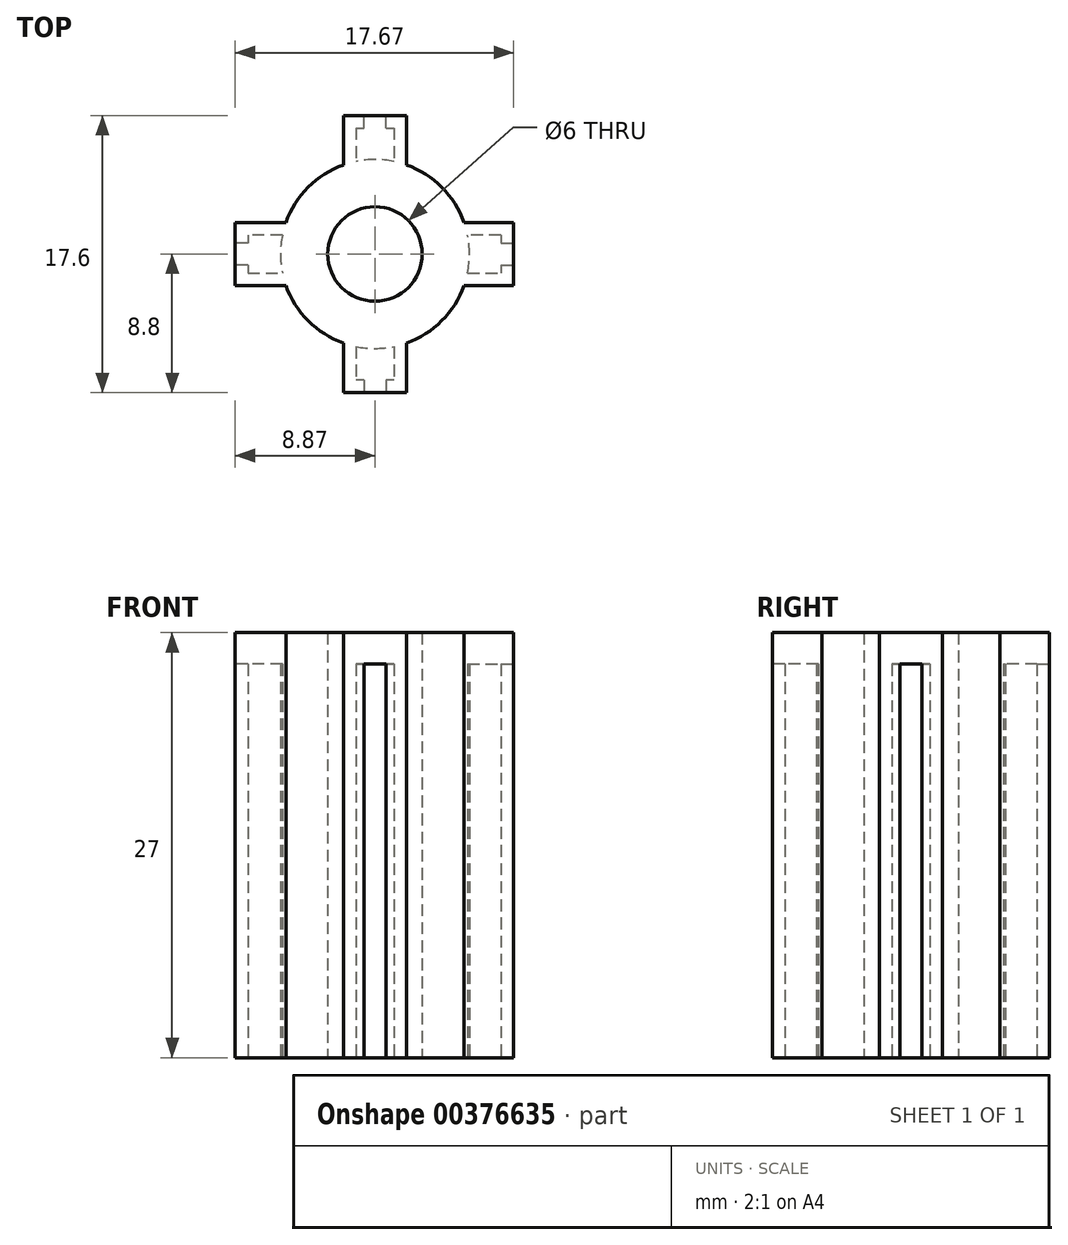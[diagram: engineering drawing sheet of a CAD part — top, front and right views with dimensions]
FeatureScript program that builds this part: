
annotation { "Feature Type Name" : "Feature", "Feature Type Description" : "" }
export const myFeature = defineFeature(function(context is Context, id is Id, definition is map)
    precondition{}
    {
        {
            var Q0;
            Q0=qCreatedBy(makeId("Top.planeOp"),FACE);
            var sketch = newSketch(context, id + "F0", { "sketchPlane" : qUnion([Q0])});
            skCircle(sketch, "E0", {"center": v(0, 0) * mm, "radius": 3 * mm});
            skArc(sketch, "E1", {"start": v(-5.88, 1.2) * mm, "mid": v(-6, 0) * mm, "end": v(-5.88, -1.2) * mm});
            skLineSegment(sketch, "E2.bottom", {"start": v(-8, -1.2) * mm, "end": v(-5.88, -1.2) * mm});
            skLineSegment(sketch, "E2.top", {"start": v(-8, -2) * mm, "end": v(-5.66, -2) * mm});
            skLineSegment(sketch, "E3.bottom", {"start": v(8, 1.2) * mm, "end": v(5.88, 1.2) * mm});
            skLineSegment(sketch, "E3.top", {"start": v(8, 2) * mm, "end": v(5.66, 2) * mm});
            skLineSegment(sketch, "E4.trimOffspring", {"start": v(-5.66, 2) * mm, "end": v(-8.07, 2) * mm});
            skLineSegment(sketch, "E5.trimOffspring", {"start": v(-5.88, 1.2) * mm, "end": v(-8.07, 1.2) * mm});
            skLineSegment(sketch, "E6.trimOffspring", {"start": v(5.88, -1.2) * mm, "end": v(8, -1.2) * mm});
            skLineSegment(sketch, "E7.trimOffspring", {"start": v(5.66, -2) * mm, "end": v(8, -2) * mm});
            skArc(sketch, "E8.trimOffspring", {"start": v(-5.66, -2) * mm, "mid": v(-4.24, -4.24) * mm, "end": v(-2, -5.66) * mm});
            skArc(sketch, "E9.trimOffspring", {"start": v(5.88, -1.2) * mm, "mid": v(6, 0) * mm, "end": v(5.88, 1.2) * mm});
            skArc(sketch, "E10.trimOffspring", {"start": v(5.66, 2) * mm, "mid": v(4.24, 4.24) * mm, "end": v(2, 5.66) * mm});
            skLineSegment(sketch, "E11.left", {"start": v(-1.2, 8) * mm, "end": v(-1.2, 5.88) * mm});
            skLineSegment(sketch, "E11.right", {"start": v(-2, 8) * mm, "end": v(-2, 5.66) * mm});
            skLineSegment(sketch, "E12.left", {"start": v(1.2, 8) * mm, "end": v(1.2, 5.88) * mm});
            skLineSegment(sketch, "E12.right", {"start": v(2, 8) * mm, "end": v(2, 5.66) * mm});
            skLineSegment(sketch, "E13.trimOffspring", {"start": v(-1.2, -5.88) * mm, "end": v(-1.2, -8) * mm});
            skLineSegment(sketch, "E14.trimOffspring", {"start": v(-2, -5.66) * mm, "end": v(-2, -8) * mm});
            skLineSegment(sketch, "E15.trimOffspring", {"start": v(1.2, -5.88) * mm, "end": v(1.2, -8) * mm});
            skLineSegment(sketch, "E16.trimOffspring", {"start": v(2, -5.66) * mm, "end": v(2, -8) * mm});
            skArc(sketch, "E17.trimOffspring", {"start": v(1.2, 5.88) * mm, "mid": v(0, 6) * mm, "end": v(-1.2, 5.88) * mm});
            skArc(sketch, "E18.trimOffspring", {"start": v(-2, 5.66) * mm, "mid": v(-4.24, 4.24) * mm, "end": v(-5.66, 2) * mm});
            skArc(sketch, "E19.trimOffspring", {"start": v(-1.2, -5.88) * mm, "mid": v(0, -6) * mm, "end": v(1.2, -5.88) * mm});
            skArc(sketch, "E20.trimOffspring", {"start": v(2, -5.66) * mm, "mid": v(4.24, -4.24) * mm, "end": v(5.66, -2) * mm});
            skLineSegment(sketch, "E21.bottom", {"start": v(8, 2) * mm, "end": v(8.8, 2) * mm});
            skLineSegment(sketch, "E21.top", {"start": v(8, -2) * mm, "end": v(8.8, -2) * mm});
            skLineSegment(sketch, "E21.left", {"start": v(8, 1.2) * mm, "end": v(8, 0.7) * mm});
            skLineSegment(sketch, "E21.right", {"start": v(8.8, 2) * mm, "end": v(8.8, 0.7) * mm});
            skLineSegment(sketch, "E22.bottom", {"start": v(-1.2, 8) * mm, "end": v(-0.7, 8) * mm});
            skLineSegment(sketch, "E22.top", {"start": v(-2, 8.8) * mm, "end": v(-0.7, 8.8) * mm});
            skLineSegment(sketch, "E22.left", {"start": v(-2, 8) * mm, "end": v(-2, 8.8) * mm});
            skLineSegment(sketch, "E22.right", {"start": v(2, 8) * mm, "end": v(2, 8.8) * mm});
            skLineSegment(sketch, "E23.bottom", {"start": v(-8.07, 2) * mm, "end": v(-8.87, 2) * mm});
            skLineSegment(sketch, "E23.top", {"start": v(-8.07, -2) * mm, "end": v(-8.87, -2) * mm});
            skLineSegment(sketch, "E23.left", {"start": v(-8.07, 1.2) * mm, "end": v(-8.07, 0.7) * mm});
            skLineSegment(sketch, "E23.right", {"start": v(-8.87, 2) * mm, "end": v(-8.87, 0.7) * mm});
            skLineSegment(sketch, "E24.bottom", {"start": v(1.2, -8) * mm, "end": v(0.7, -8) * mm});
            skLineSegment(sketch, "E24.top", {"start": v(2, -8.8) * mm, "end": v(0.7, -8.8) * mm});
            skLineSegment(sketch, "E24.left", {"start": v(2, -8) * mm, "end": v(2, -8.8) * mm});
            skLineSegment(sketch, "E24.right", {"start": v(-2, -8) * mm, "end": v(-2, -8.8) * mm});
            skLineSegment(sketch, "E25", {"start": v(0.7, -8) * mm, "end": v(0.7, -8.8) * mm});
            skLineSegment(sketch, "E26", {"start": v(-0.7, -8) * mm, "end": v(-0.7, -8.8) * mm});
            skLineSegment(sketch, "E27.trimOffspring", {"start": v(-0.7, -8) * mm, "end": v(-1.2, -8) * mm});
            skLineSegment(sketch, "E28.trimOffspring", {"start": v(-0.7, -8.8) * mm, "end": v(-2, -8.8) * mm});
            skLineSegment(sketch, "E29", {"start": v(8, 0.7) * mm, "end": v(8.8, 0.7) * mm});
            skLineSegment(sketch, "E30", {"start": v(8, -0.7) * mm, "end": v(8.8, -0.7) * mm});
            skLineSegment(sketch, "E31", {"start": v(-0.7, 8) * mm, "end": v(-0.7, 8.8) * mm});
            skLineSegment(sketch, "E32", {"start": v(0.7, 8) * mm, "end": v(0.7, 8.8) * mm});
            skLineSegment(sketch, "E33.trimOffspring", {"start": v(0.7, 8) * mm, "end": v(1.2, 8) * mm});
            skLineSegment(sketch, "E34.trimOffspring", {"start": v(0.7, 8.8) * mm, "end": v(2, 8.8) * mm});
            skLineSegment(sketch, "E35", {"start": v(-8.07, 0.7) * mm, "end": v(-8.87, 0.7) * mm});
            skLineSegment(sketch, "E36", {"start": v(-8.07, -0.7) * mm, "end": v(-8.87, -0.7) * mm});
            skLineSegment(sketch, "E37", {"start": v(-8, -1.2) * mm, "end": v(-8.07, -1.2) * mm});
            skLineSegment(sketch, "E38", {"start": v(-8, -2) * mm, "end": v(-8.07, -2) * mm});
            skLineSegment(sketch, "E39.trimOffspring", {"start": v(-8.07, -0.7) * mm, "end": v(-8.07, -1.2) * mm});
            skLineSegment(sketch, "E40.trimOffspring", {"start": v(-8.87, -0.7) * mm, "end": v(-8.87, -2) * mm});
            skLineSegment(sketch, "E41.trimOffspring", {"start": v(8.8, -0.7) * mm, "end": v(8.8, -2) * mm});
            skLineSegment(sketch, "E42.trimOffspring", {"start": v(8, -0.7) * mm, "end": v(8, -1.2) * mm});
            skSolve(sketch);
        }
        {
            var Q0;
            Q0=makeQuery(id+"F0.imprint","IMPRINT",FACE,{"disambiguationData":[TD([[makeQuery(id+"F0.imprint","IMPRINT",EDGE,{"derivedFrom":sQuery(id+"F0.wireOp",EDGE,"E0")}),-1.0]])]});
            extrude(context, id + "F1", {"entities" : qUnion([Q0]), "depth" : 25 * mm});
        }
        {
            var Q0;
            Q0=makeQuery(id+"F1.opExtrude","CAP_FACE",FACE,{"disambiguationData":[OSD([sQuery(id+"F0.wireOp",EDGE,"E0"),sQuery(id+"F0.wireOp",EDGE,"E1"),sQuery(id+"F0.wireOp",EDGE,"E2.bottom"),sQuery(id+"F0.wireOp",EDGE,"E2.top"),sQuery(id+"F0.wireOp",EDGE,"E3.bottom"),sQuery(id+"F0.wireOp",EDGE,"E3.top"),sQuery(id+"F0.wireOp",EDGE,"E4.trimOffspring"),sQuery(id+"F0.wireOp",EDGE,"E5.trimOffspring"),sQuery(id+"F0.wireOp",EDGE,"E6.trimOffspring"),sQuery(id+"F0.wireOp",EDGE,"E7.trimOffspring"),sQuery(id+"F0.wireOp",EDGE,"E8.trimOffspring"),sQuery(id+"F0.wireOp",EDGE,"E9.trimOffspring"),sQuery(id+"F0.wireOp",EDGE,"E10.trimOffspring"),sQuery(id+"F0.wireOp",EDGE,"E11.left"),sQuery(id+"F0.wireOp",EDGE,"E11.right"),sQuery(id+"F0.wireOp",EDGE,"E12.left"),sQuery(id+"F0.wireOp",EDGE,"E12.right"),sQuery(id+"F0.wireOp",EDGE,"E13.trimOffspring"),sQuery(id+"F0.wireOp",EDGE,"E14.trimOffspring"),sQuery(id+"F0.wireOp",EDGE,"E15.trimOffspring"),sQuery(id+"F0.wireOp",EDGE,"E16.trimOffspring"),sQuery(id+"F0.wireOp",EDGE,"E17.trimOffspring"),sQuery(id+"F0.wireOp",EDGE,"E18.trimOffspring"),sQuery(id+"F0.wireOp",EDGE,"E19.trimOffspring"),sQuery(id+"F0.wireOp",EDGE,"E20.trimOffspring"),sQuery(id+"F0.wireOp",EDGE,"E21.bottom"),sQuery(id+"F0.wireOp",EDGE,"E21.top"),sQuery(id+"F0.wireOp",EDGE,"E21.left"),sQuery(id+"F0.wireOp",EDGE,"E21.right"),sQuery(id+"F0.wireOp",EDGE,"E22.bottom"),sQuery(id+"F0.wireOp",EDGE,"E22.top"),sQuery(id+"F0.wireOp",EDGE,"E22.left"),sQuery(id+"F0.wireOp",EDGE,"E22.right"),sQuery(id+"F0.wireOp",EDGE,"E23.bottom"),sQuery(id+"F0.wireOp",EDGE,"E23.top"),sQuery(id+"F0.wireOp",EDGE,"E23.left"),sQuery(id+"F0.wireOp",EDGE,"E23.right"),sQuery(id+"F0.wireOp",EDGE,"E24.bottom"),sQuery(id+"F0.wireOp",EDGE,"E24.top"),sQuery(id+"F0.wireOp",EDGE,"E24.left"),sQuery(id+"F0.wireOp",EDGE,"E24.right"),sQuery(id+"F0.wireOp",EDGE,"E25"),sQuery(id+"F0.wireOp",EDGE,"E26"),sQuery(id+"F0.wireOp",EDGE,"E27.trimOffspring"),sQuery(id+"F0.wireOp",EDGE,"E28.trimOffspring"),sQuery(id+"F0.wireOp",EDGE,"E29"),sQuery(id+"F0.wireOp",EDGE,"E30"),sQuery(id+"F0.wireOp",EDGE,"E31"),sQuery(id+"F0.wireOp",EDGE,"E32"),sQuery(id+"F0.wireOp",EDGE,"E33.trimOffspring"),sQuery(id+"F0.wireOp",EDGE,"E34.trimOffspring"),sQuery(id+"F0.wireOp",EDGE,"E35"),sQuery(id+"F0.wireOp",EDGE,"E36"),sQuery(id+"F0.wireOp",EDGE,"E37"),sQuery(id+"F0.wireOp",EDGE,"E38"),sQuery(id+"F0.wireOp",EDGE,"E39.trimOffspring"),sQuery(id+"F0.wireOp",EDGE,"E40.trimOffspring"),sQuery(id+"F0.wireOp",EDGE,"E41.trimOffspring"),sQuery(id+"F0.wireOp",EDGE,"E42.trimOffspring")])],"isStart":false});
            var sketch = newSketch(context, id + "F2", { "sketchPlane" : qUnion([Q0])});
            skArc(sketch, "E43", {"start": v(-5.66, -2) * mm, "mid": v(-4.24, -4.24) * mm, "end": v(-2, -5.66) * mm});
            skLineSegment(sketch, "E44.top", {"start": v(-2, 8.8) * mm, "end": v(2, 8.8) * mm});
            skLineSegment(sketch, "E44.left", {"start": v(-2, 5.66) * mm, "end": v(-2, 8.8) * mm});
            skLineSegment(sketch, "E44.right", {"start": v(2, 5.66) * mm, "end": v(2, 8.8) * mm});
            skLineSegment(sketch, "E45.bottom", {"start": v(5.66, 2) * mm, "end": v(8.8, 2) * mm});
            skLineSegment(sketch, "E45.top", {"start": v(5.66, -2) * mm, "end": v(8.8, -2) * mm});
            skLineSegment(sketch, "E45.right", {"start": v(8.8, 2) * mm, "end": v(8.8, -2) * mm});
            skLineSegment(sketch, "E46.top", {"start": v(2, -8.8) * mm, "end": v(-2, -8.8) * mm});
            skLineSegment(sketch, "E46.left", {"start": v(2, -5.66) * mm, "end": v(2, -8.8) * mm});
            skLineSegment(sketch, "E46.right", {"start": v(-2, -5.66) * mm, "end": v(-2, -8.8) * mm});
            skLineSegment(sketch, "E47.bottom", {"start": v(-5.66, -2) * mm, "end": v(-8.87, -2) * mm});
            skLineSegment(sketch, "E47.top", {"start": v(-5.66, 2) * mm, "end": v(-8.87, 2) * mm});
            skLineSegment(sketch, "E47.right", {"start": v(-8.87, -2) * mm, "end": v(-8.87, 2) * mm});
            skArc(sketch, "E48.trimOffspring", {"start": v(-2, 5.66) * mm, "mid": v(-4.24, 4.24) * mm, "end": v(-5.66, 2) * mm});
            skArc(sketch, "E49.trimOffspring", {"start": v(5.66, 2) * mm, "mid": v(4.24, 4.24) * mm, "end": v(2, 5.66) * mm});
            skArc(sketch, "E50.trimOffspring", {"start": v(2, -5.66) * mm, "mid": v(4.24, -4.24) * mm, "end": v(5.66, -2) * mm});
            skCircle(sketch, "E51", {"center": v(0, 0) * mm, "radius": 3 * mm});
            skSolve(sketch);
        }
        {
            var Q0;
            Q0 = qSketchRegion(id + "F2", true);
            extrude(context, id + "F3", {"entities" : qUnion([Q0]), "operationType" : NewBodyOperationType.ADD, "depth" : 2 * mm});
        }
    });
